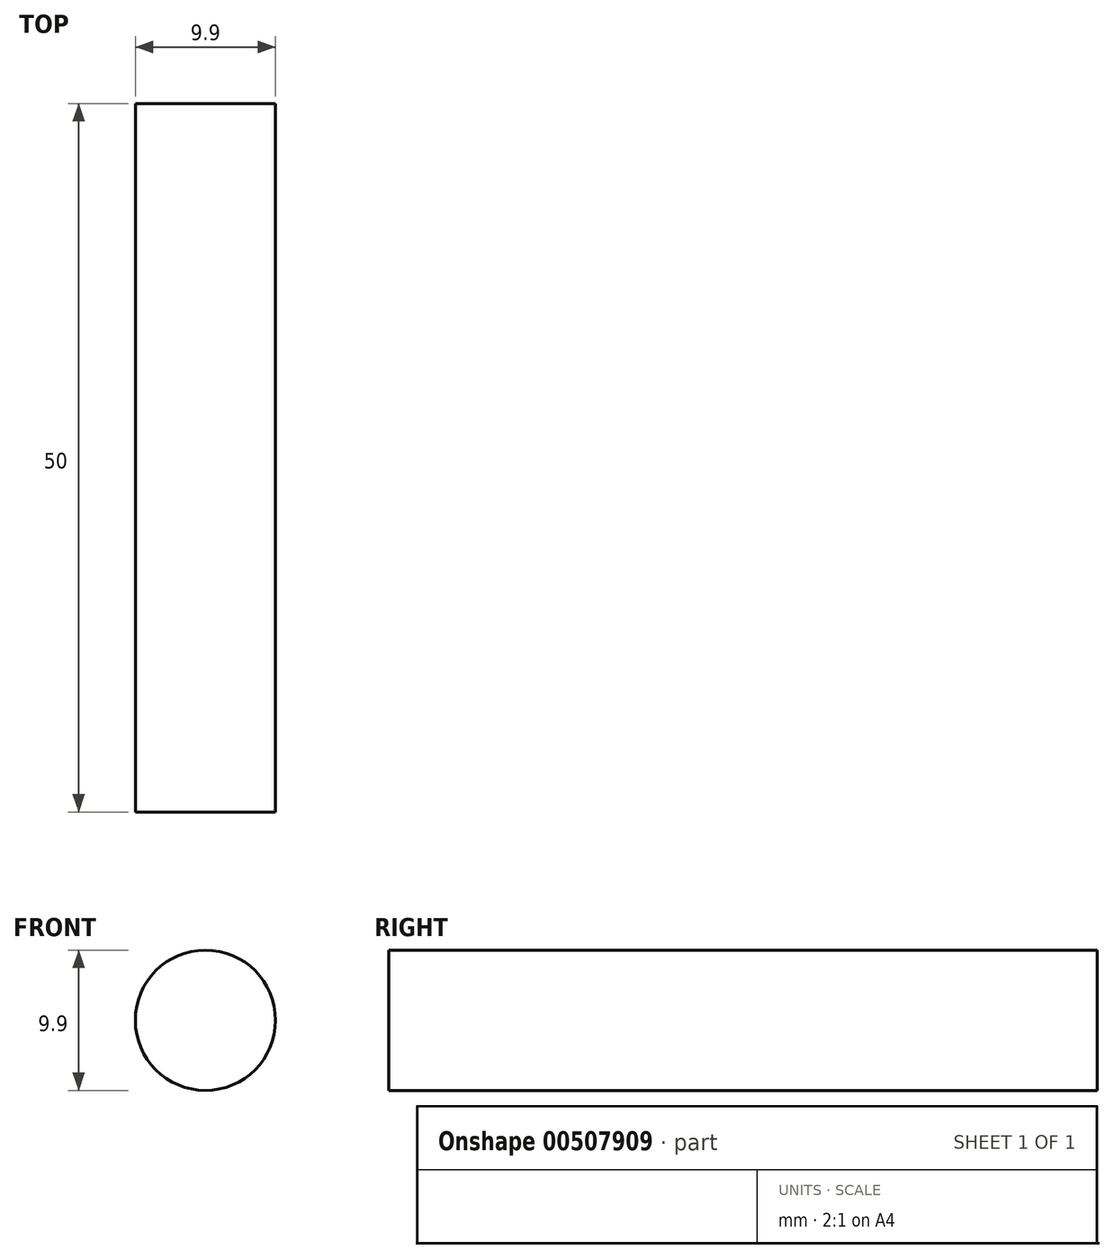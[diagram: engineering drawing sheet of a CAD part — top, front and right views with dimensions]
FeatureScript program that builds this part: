
annotation { "Feature Type Name" : "Feature", "Feature Type Description" : "" }
export const myFeature = defineFeature(function(context is Context, id is Id, definition is map)
    precondition{}
    {
        {
            var Q0;
            Q0=qCreatedBy(makeId("Front.planeOp"),FACE);
            var sketch = newSketch(context, id + "F0", { "sketchPlane" : qUnion([Q0])});
            skCircle(sketch, "E0", {"center": v(0, 0) * mm, "radius": 4.95 * mm});
            skSolve(sketch);
        }
        {
            var Q0;
            Q0=makeQuery(id+"F0.imprint","IMPRINT",FACE,{"disambiguationData":[TD([[makeQuery(id+"F0.imprint","IMPRINT",EDGE,{"derivedFrom":sQuery(id+"F0.wireOp",EDGE,"E0")}),1.0]])]});
            var Q1;
            Q1=sQuery(id+"F0.wireOp",EDGE,"E0");
            extrude(context, id + "F1", {"entities" : qUnion([Q0]), "surfaceEntities" : qUnion([Q1]), "depth" : 50 * mm});
        }
    });
